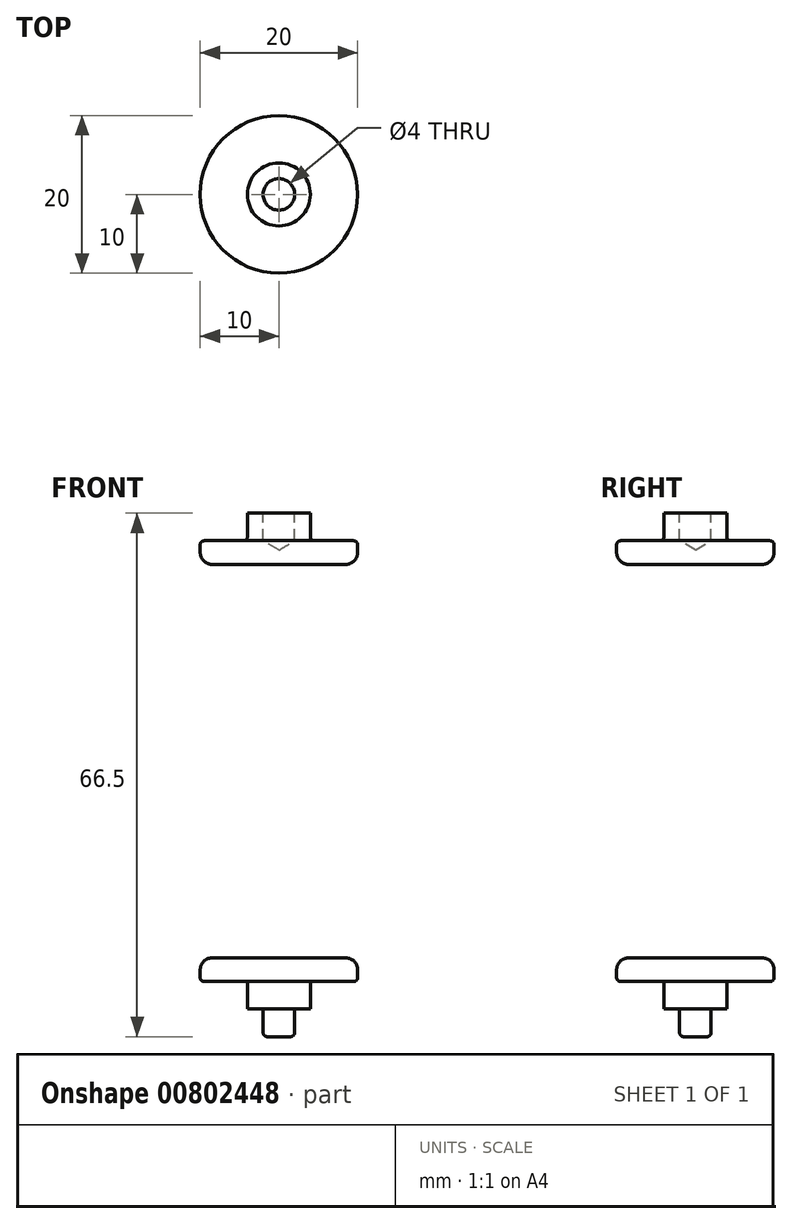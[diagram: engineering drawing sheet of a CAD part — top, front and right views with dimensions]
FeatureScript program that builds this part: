
annotation { "Feature Type Name" : "Feature", "Feature Type Description" : "" }
export const myFeature = defineFeature(function(context is Context, id is Id, definition is map)
    precondition{}
    {
        {
            var Q0;
            Q0=qCreatedBy(makeId("Top.planeOp"),FACE);
            var sketch = newSketch(context, id + "F0", { "sketchPlane" : qUnion([Q0])});
            skCircle(sketch, "E0", {"center": v(0, 0) * mm, "radius": 10 * mm});
            skCircle(sketch, "E1", {"center": v(0, 0) * mm, "radius": 4 * mm});
            skSolve(sketch);
        }
        {
            var Q0;
            Q0=qSketchRegion(id+"F0",true);
            var Q1;
            Q1=makeQuery(id+"F0.imprint","IMPRINT",FACE,{"disambiguationData":[TD([[makeQuery(id+"F0.imprint","IMPRINT",EDGE,{"derivedFrom":sQuery(id+"F0.wireOp",EDGE,"E1")}),1.0]])]});
            extrude(context, id + "F1", {"entities" : qUnion([Q0, Q1]), "depth" : 3 * mm, "offsetDistance" : 25 * mm});
        }
        {
            var Q0;
            Q0=makeQuery(id+"F0.imprint","IMPRINT",FACE,{"disambiguationData":[TD([[makeQuery(id+"F0.imprint","IMPRINT",EDGE,{"derivedFrom":sQuery(id+"F0.wireOp",EDGE,"E1")}),1.0]])]});
            extrude(context, id + "F2", {"entities" : qUnion([Q0]), "operationType" : NewBodyOperationType.ADD, "oppositeDirection" : true, "depth" : 3.5 * mm, "offsetDistance" : 25 * mm});
        }
        {
            var Q0;
            Q0=makeQuery(id+"F1.opExtrude","CAP_FACE",FACE,{"disambiguationData":[OSD([sQuery(id+"F0.wireOp",EDGE,"E0")])],"isStart":false});
            cPlane(context, id + "F3", {"entities" : qUnion([Q0]), "cplaneType" : CPlaneType.OFFSET, "offset" : 25 * mm, "width" : 150 * mm, "height" : 150 * mm});
        }
        {
            var Q0;
            Q0=makeQuery(id+"F1.opExtrude","SWEPT_BODY",BODY,{"disambiguationData":[OSD([sQuery(id+"F0.wireOp",EDGE,"E0")])]});
            var Q1;
            Q1=qCreatedBy(id+"F3.planeOp",FACE);
            mirror(context, id + "F4", {"entities" : qUnion([Q0]), "mirrorPlane" : qUnion([Q1])});
        }
        {
            var Q0;
            Q0=makeQuery(id+"F2.opExtrude","CAP_FACE",FACE,{"disambiguationData":[OSD([sQuery(id+"F0.wireOp",EDGE,"E1")])],"isStart":false});
            var sketch = newSketch(context, id + "F5", { "sketchPlane" : qUnion([Q0])});
            skCircle(sketch, "E2", {"center": v(0, 0) * mm, "radius": 2 * mm});
            skSolve(sketch);
        }
        {
            var Q0;
            Q0=qSketchRegion(id+"F5",true);
            extrude(context, id + "F6", {"entities" : qUnion([Q0]), "operationType" : NewBodyOperationType.ADD, "depth" : 3.5 * mm, "offsetDistance" : 25 * mm});
        }
        {
            var Q0;
            Q0=makeQuery(id+"F4.opPattern","COPY",FACE,{"derivedFrom":makeQuery(id+"F2.opExtrude","CAP_FACE",FACE,{"disambiguationData":[OSD([sQuery(id+"F0.wireOp",EDGE,"E1")])],"isStart":false}),"instanceName":"1"});
            var sketch = newSketch(context, id + "F7", { "sketchPlane" : qUnion([Q0])});
            skPoint(sketch, "E3", {"position": v(0, 0) * mm});
            skSolve(sketch);
        }
        {
            var Q0;
            Q0=sQuery(id+"F7.wireOp",VERTEX,"E3");
            var Q1;
            Q1=makeQuery(id+"F4.opPattern","COPY",BODY,{"derivedFrom":makeQuery(id+"F1.opExtrude","SWEPT_BODY",BODY,{"disambiguationData":[OSD([sQuery(id+"F0.wireOp",EDGE,"E0")])]}),"instanceName":"1"});
            hole(context, id + "F8", {"style" : HoleStyle.SIMPLE, "endStyle" : HoleEndStyle.BLIND, "holeDiameter" : 4 * mm, "majorDiameter" : 5 * mm, "holeDepth" : 3.5 * mm, "isTappedThrough" : true, "tappedDepth" : 12 * mm, "tapClearance" : 3, "locations" : qUnion([Q0]), "scope" : qUnion([Q1])});
        }
        {
            var Q0;
            Q0=makeQuery(id+"F8.hole-0.boolean.opBoolean","COPY",EDGE,{"derivedFrom":makeQuery(id+"F8.hole-0.opRevolve","SWEPT_EDGE",EDGE,{"disambiguationData":[OSD([sQuery(id+"F8.hole-0.sketch.wireOp",EDGE,"core_line_2"),sQuery(id+"F8.hole-0.sketch.wireOp",EDGE,"core_line_3")])]})});
            var Q1;
            Q1=makeQuery(id+"F4.opPattern","COPY",FACE,{"derivedFrom":makeQuery(id+"F1.opExtrude","CAP_FACE",FACE,{"disambiguationData":[OSD([sQuery(id+"F0.wireOp",EDGE,"E0")])],"isStart":true}),"instanceName":"1"});
            var Q2;
            Q2=makeQuery(id+"F6.opExtrude","CAP_EDGE",EDGE,{"disambiguationData":[OSD([sQuery(id+"F5.wireOp",EDGE,"E2")])],"isStart":false});
            var Q3;
            Q3=makeQuery(id+"F6.opExtrude","CAP_EDGE",EDGE,{"disambiguationData":[OSD([sQuery(id+"F5.wireOp",EDGE,"E2")])],"isStart":true});
            var Q4;
            Q4=makeQuery(id+"F2.opExtrude","CAP_EDGE",EDGE,{"disambiguationData":[OSD([sQuery(id+"F0.wireOp",EDGE,"E1")])],"isStart":true});
            var Q5;
            Q5=makeQuery(id+"F1.opExtrude","CAP_EDGE",EDGE,{"disambiguationData":[OSD([sQuery(id+"F0.wireOp",EDGE,"E0")])],"isStart":true});
            fillet(context, id + "F9", {"entities" : qUnion([Q0, Q1, Q2, Q3, Q4, Q5]), "radius" : .5 * mm, "tangentPropagation" : true, "allowEdgeOverflow" : false});
        }
        {
            var Q0;
            Q0=makeQuery(id+"F1.opExtrude","CAP_EDGE",EDGE,{"disambiguationData":[OSD([sQuery(id+"F0.wireOp",EDGE,"E0")])],"isStart":false});
            var Q1;
            Q1=makeQuery(id+"F4.opPattern","COPY",EDGE,{"derivedFrom":makeQuery(id+"F1.opExtrude","CAP_EDGE",EDGE,{"disambiguationData":[OSD([sQuery(id+"F0.wireOp",EDGE,"E0")])],"isStart":false}),"instanceName":"1"});
            fillet(context, id + "F10", {"entities" : qUnion([Q0, Q1]), "radius" : 1.5 * mm, "tangentPropagation" : true, "allowEdgeOverflow" : false});
        }
    });
